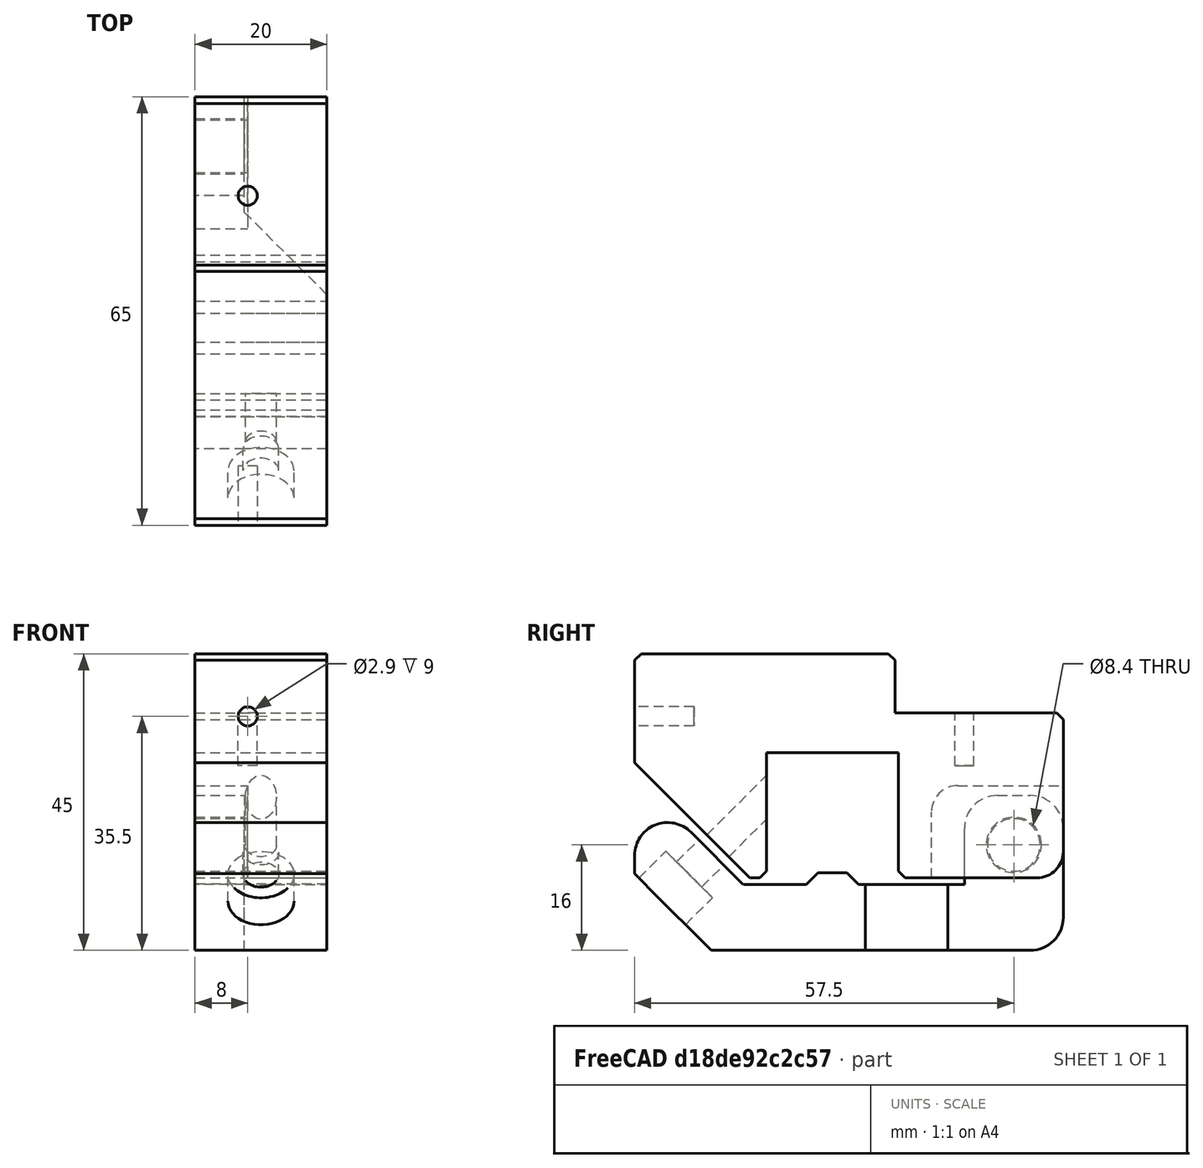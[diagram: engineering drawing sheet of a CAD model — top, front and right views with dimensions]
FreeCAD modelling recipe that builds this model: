
FCSTD DOCUMENT  (FreeCAD 0.18.4R)
Label: 0816_adaptor_16mm
License: All rights reserved
LicenseURL: http://en.wikipedia.org/wiki/All_rights_reserved
objects: Part::Box×14, Part::Cut×10, Part::Cylinder×7, Part::MultiFuse×6, Part::Chamfer×3, Part::Fillet×2
note: 42 computed .brp shape members not serialized (recipe doc carries the construction recipe); baked Part::Feature solids carry a one-line shape summary decoded from their .brp

FEATURE [Part::Box] Box  label="Cube"
  AttacherType = Attacher::AttachEngine3D
  Height = 20
  Length = 20
  Width = 20
FEATURE [Part::Box] Box001  label="Cube_base"
  AttacherType = Attacher::AttachEngine3D
  Height = 35
  Length = 20
  Placement = pos=(0,-20,0) rot=(0,0,1;0rad)
  Width = 65
FEATURE [Part::Box] Box002  label="Cube002"
  AttacherType = Attacher::AttachEngine3D
  Height = 9
  Length = 20
  Placement = pos=(0,19.5,26) rot=(0,0,1;0rad)
  Width = 25.5
FEATURE [Part::Cylinder] Cylinder
  Angle = 360
  AttacherType = Attacher::AttachEngine3D
  Height = 10
  Placement = pos=(8,30,18) rot=(0,0,1;0rad)
  Radius = 1.45
FEATURE [Part::Cylinder] Cylinder001
  Angle = 360
  AttacherType = Attacher::AttachEngine3D
  Height = 15
  Placement = pos=(10,-8.89949,4.34315) rot=(-1,0,0;0.785398rad)
  Radius = 2.35
FEATURE [Part::Cylinder] Cylinder002
  Angle = 360
  AttacherType = Attacher::AttachEngine3D
  Height = 10
  Placement = pos=(8,-11,25.5) rot=(1,0,0;1.5708rad)
  Radius = 1.45
FEATURE [Part::Box] Box003  label="cube_45deg"
  AttacherType = Attacher::AttachEngine3D
  Height = 50
  Length = 20
  Placement = pos=(0,-18.4853,-18.3848) rot=(1,0,0;0.785398rad)
  Width = 25
FEATURE [Part::MultiFuse] Fusion
  Shapes = -> [Box,Box002,Box003]
FEATURE [Part::Cut] Cut
  Base = -> Box001
  Tool = -> Fusion
FEATURE [Part::Box] Box004  label="Cube003"
  AttacherType = Attacher::AttachEngine3D
  Height = 15
  Length = 8
  Placement = pos=(0,25,0) rot=(0,0,1;0rad)
  Width = 20
FEATURE [Part::Cut] Cut001
  Base = -> Cut
  Tool = -> Box004
FEATURE [Part::Cylinder] Cylinder004
  Angle = 360
  AttacherType = Attacher::AttachEngine3D
  Height = 10
  Placement = pos=(-1.1e-15,37.5,6) rot=(0,1,0;1.5708rad)
  Radius = 4
FEATURE [Part::Box] Box005  label="Cube004"
  AttacherType = Attacher::AttachEngine3D
  Height = 10
  Length = 7.5
  Placement = pos=(0,-20,-10) rot=(0,0,1;0rad)
  Width = 65
FEATURE [Part::Box] Box006  label="Cube005+"
  AttacherType = Attacher::AttachEngine3D
  Height = 14
  Length = 7.5
  Placement = pos=(0,30,-0.5) rot=(0,0,1;0rad)
  Width = 15
FEATURE [Part::MultiFuse] Fusion001  label="fusion holes"
  Shapes = -> [Cylinder,Cylinder002,Cylinder001]
FEATURE [Part::Cut] Cut002
  Base = -> Cut001
  Tool = -> Fusion001
FEATURE [Part::MultiFuse] Fusion002
  Shapes = -> [Cut002,Cylinder004]
FEATURE [Part::Cylinder] Cylinder005  label="Cylinder005-"
  Angle = 360
  AttacherType = Attacher::AttachEngine3D
  Height = 10
  Placement = pos=(-1.1e-15,37.5,6) rot=(0,1,0;1.5708rad)
  Radius = 4.2
FEATURE [Part::MultiFuse] Fusion003
  Shapes = -> [Box005,Box006]
FEATURE [Part::Cut] Cut003
  Base = -> Fusion003
  Tool = -> Cylinder005
FEATURE [Part::Box] Box007  label="Cube006"
  AttacherType = Attacher::AttachEngine3D
  Height = 30
  Length = 20
  Placement = pos=(0,-20,-0.5) rot=(0,0,1;0rad)
  Width = 20
FEATURE [Part::Box] Box008  label="Cube007"
  AttacherType = Attacher::AttachEngine3D
  Height = 50
  Length = 20
  Placement = pos=(0,-3.53553,0) rot=(1,0,0;0.785398rad)
  Width = 30
FEATURE [Part::Cut] Cut004
  Base = -> Box007
  Tool = -> Box008
FEATURE [Part::Box] Box009  label="Cube008-"
  AttacherType = Attacher::AttachEngine3D
  Height = 10
  Length = 20
  Placement = pos=(0,-3.5,-0.5) rot=(0,0,1;0rad)
  Width = 10
FEATURE [Part::Cut] Cut005
  Base = -> Cut004
  Tool = -> Box009
FEATURE [Part::Cylinder] Cylinder006  label="Cylinder006-"
  Angle = 360
  AttacherType = Attacher::AttachEngine3D
  Height = 20
  Placement = pos=(10,-22.3345,-9.09188) rot=(-1,0,0;0.785398rad)
  Radius = 2.7
FEATURE [Part::Box] Box010  label="Cube009+"
  AttacherType = Attacher::AttachEngine3D
  Height = 10
  Length = 12.5
  Placement = pos=(7.5,-20,-10) rot=(0,0,1;0rad)
  Width = 35
FEATURE [Part::MultiFuse] Fusion004
  Shapes = -> [Box010,Cut005,Cut003]
FEATURE [Part::Cut] Cut006
  Base = -> Fusion004
  Tool = -> Cylinder006
FEATURE [Part::Box] Box011  label="Cube008-001"
  AttacherType = Attacher::AttachEngine3D
  Height = 50
  Length = 20
  Placement = pos=(0,-24.0416,-36.7696) rot=(1,0,0;0.785398rad)
  Width = 30
FEATURE [Part::Cut] Cut007
  Base = -> Cut006
  Tool = -> Box011
FEATURE [Part::Box] Box012  label="Cube008"
  AttacherType = Attacher::AttachEngine3D
  Height = 1
  Length = 20
  Placement = pos=(0,-20,0) rot=(0,0,1;0rad)
  Width = 65
FEATURE [Part::Cut] Cut008  label="cut xxx"
  Base = -> Fusion002
  Tool = -> Box012
FEATURE [Part::Cylinder] Cylinder007  label="Cylinder006-001"
  Angle = 360
  AttacherType = Attacher::AttachEngine3D
  Height = 6
  Placement = pos=(10,-15.9706,-2.72792) rot=(-1,0,0;0.785398rad)
  Radius = 5
FEATURE [Part::Cut] Cut009  label="cutXXX"
  Base = -> Cut007
  Tool = -> Cylinder007
FEATURE [Part::Box] Box013  label="Cube009"
  AttacherType = Attacher::AttachEngine3D
  Height = 1.8
  Length = 20
  Placement = pos=(0,7.8,0) rot=(0,0,1;0rad)
  Width = 4.4
FEATURE [Part::MultiFuse] Fusion005  label="Bottom_part"
  Shapes = -> [Cut009,Box013]
FEATURE [Part::Chamfer] Chamfer
  Base = -> Cut008
  Edges = 5 edges r=1: [Edge14,Edge19,Edge42,Edge44,Edge46]
FEATURE [Part::Fillet] Fillet  label="top part"
  Base = -> Chamfer
  Edges = 2 edges r=4: [Edge3,Edge46]
FEATURE [Part::Chamfer] Chamfer001
  Base = -> Fusion005
  Edges = 4 edges r=1.79: [Edge5,Edge6,Edge11,Edge12]
FEATURE [Part::Chamfer] Chamfer002
  Base = -> Chamfer001
  Edges = 1 edges r=12.49: [Edge88]
FEATURE [Part::Fillet] Fillet001  label="bot part"
  Base = -> Chamfer002
  Edges = 4 edges r=5: [Edge17,Edge38,Edge58,Edge102]
